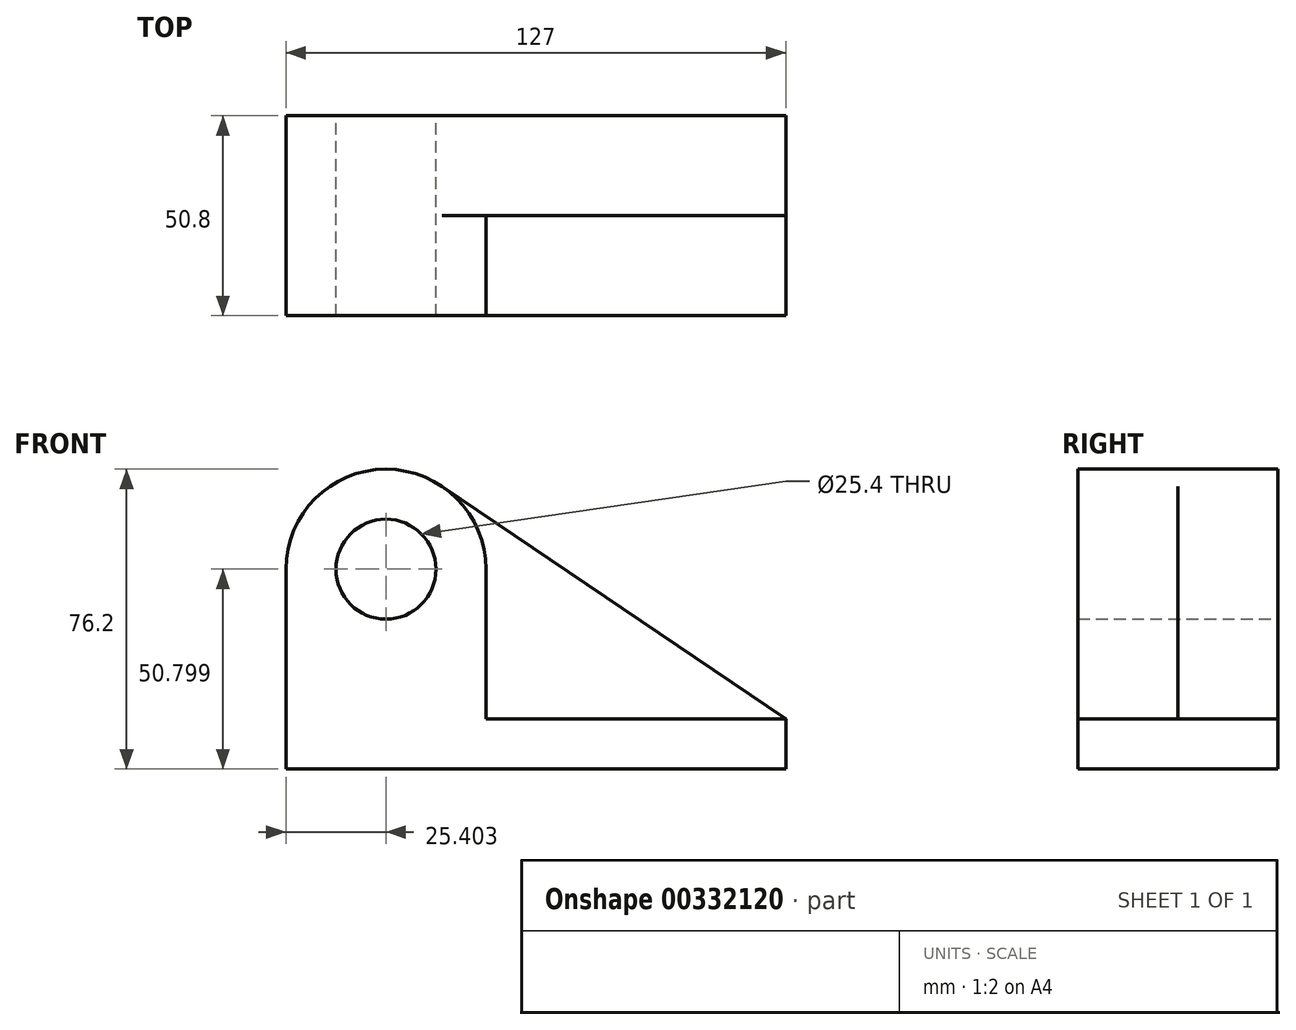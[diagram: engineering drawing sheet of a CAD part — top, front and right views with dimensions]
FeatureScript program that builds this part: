
annotation { "Feature Type Name" : "Feature", "Feature Type Description" : "" }
export const myFeature = defineFeature(function(context is Context, id is Id, definition is map)
    precondition{}
    {
        {
            var Q0;
            Q0=qCreatedBy(makeId("Front.planeOp"),FACE);
            var sketch = newSketch(context, id + "F0", { "sketchPlane" : qUnion([Q0])});
            skCircle(sketch, "E0", {"center": v(-55.92, 29.8) * mm, "radius": 12.7 * mm});
            skArc(sketch, "E1", {"start": v(-41.68, 50.83) * mm, "mid": v(-67.82, 52.24) * mm, "end": v(-81.32, 29.8) * mm});
            skLineSegment(sketch, "E2", {"start": v(-81.32, 29.8) * mm, "end": v(-81.32, -21) * mm});
            skLineSegment(sketch, "E3", {"start": v(-81.32, -21) * mm, "end": v(45.68, -21) * mm});
            skLineSegment(sketch, "E4", {"start": v(45.68, -21) * mm, "end": v(45.68, -8.3) * mm});
            skLineSegment(sketch, "E5", {"start": v(45.68, -8.3) * mm, "end": v(-41.68, 50.83) * mm});
            skSolve(sketch);
        }
        {
            var Q0;
            Q0=makeQuery(id+"F0.imprint","IMPRINT",FACE,{"disambiguationData":[TD([[makeQuery(id+"F0.imprint","IMPRINT",EDGE,{"derivedFrom":sQuery(id+"F0.wireOp",EDGE,"E0")}),-1.0]])]});
            extrude(context, id + "F1", {"entities" : qUnion([Q0]), "depth" : 25.4 * mm});
        }
        {
            var Q0;
            Q0=makeQuery(id+"F1.opExtrude","CAP_FACE",FACE,{"disambiguationData":[OSD([sQuery(id+"F0.wireOp",EDGE,"E0"),sQuery(id+"F0.wireOp",EDGE,"E1"),sQuery(id+"F0.wireOp",EDGE,"E2"),sQuery(id+"F0.wireOp",EDGE,"E3"),sQuery(id+"F0.wireOp",EDGE,"E4"),sQuery(id+"F0.wireOp",EDGE,"E5")])],"isStart":false});
            var sketch = newSketch(context, id + "F2", { "sketchPlane" : qUnion([Q0])});
            skCircle(sketch, "E6", {"center": v(-55.92, 29.8) * mm, "radius": 12.7 * mm});
            skArc(sketch, "E7", {"start": v(-30.52, 29.8) * mm, "mid": v(-55.92, 55.2) * mm, "end": v(-81.32, 29.8) * mm});
            skLineSegment(sketch, "E8.bottom", {"start": v(45.68, -8.3) * mm, "end": v(-30.52, -8.3) * mm});
            skLineSegment(sketch, "E8.top", {"start": v(45.68, -21) * mm, "end": v(-81.32, -21) * mm});
            skLineSegment(sketch, "E8.left", {"start": v(45.68, -8.3) * mm, "end": v(45.68, -21) * mm});
            skLineSegment(sketch, "E8.right", {"start": v(-81.32, -8.3) * mm, "end": v(-81.32, -21) * mm});
            skLineSegment(sketch, "E9", {"start": v(-30.52, 29.8) * mm, "end": v(-30.52, -8.3) * mm});
            skLineSegment(sketch, "E10", {"start": v(-81.32, 29.8) * mm, "end": v(-81.32, -8.3) * mm});
            skSolve(sketch);
        }
        {
            var Q0;
            Q0=makeQuery(id+"F2.imprint","IMPRINT",FACE,{"disambiguationData":[TD([[makeQuery(id+"F2.imprint","IMPRINT",EDGE,{"derivedFrom":sQuery(id+"F2.wireOp",EDGE,"E6")}),-1.0]])]});
            extrude(context, id + "F3", {"entities" : qUnion([Q0]), "operationType" : NewBodyOperationType.ADD, "depth" : 25.4 * mm});
        }
    });
